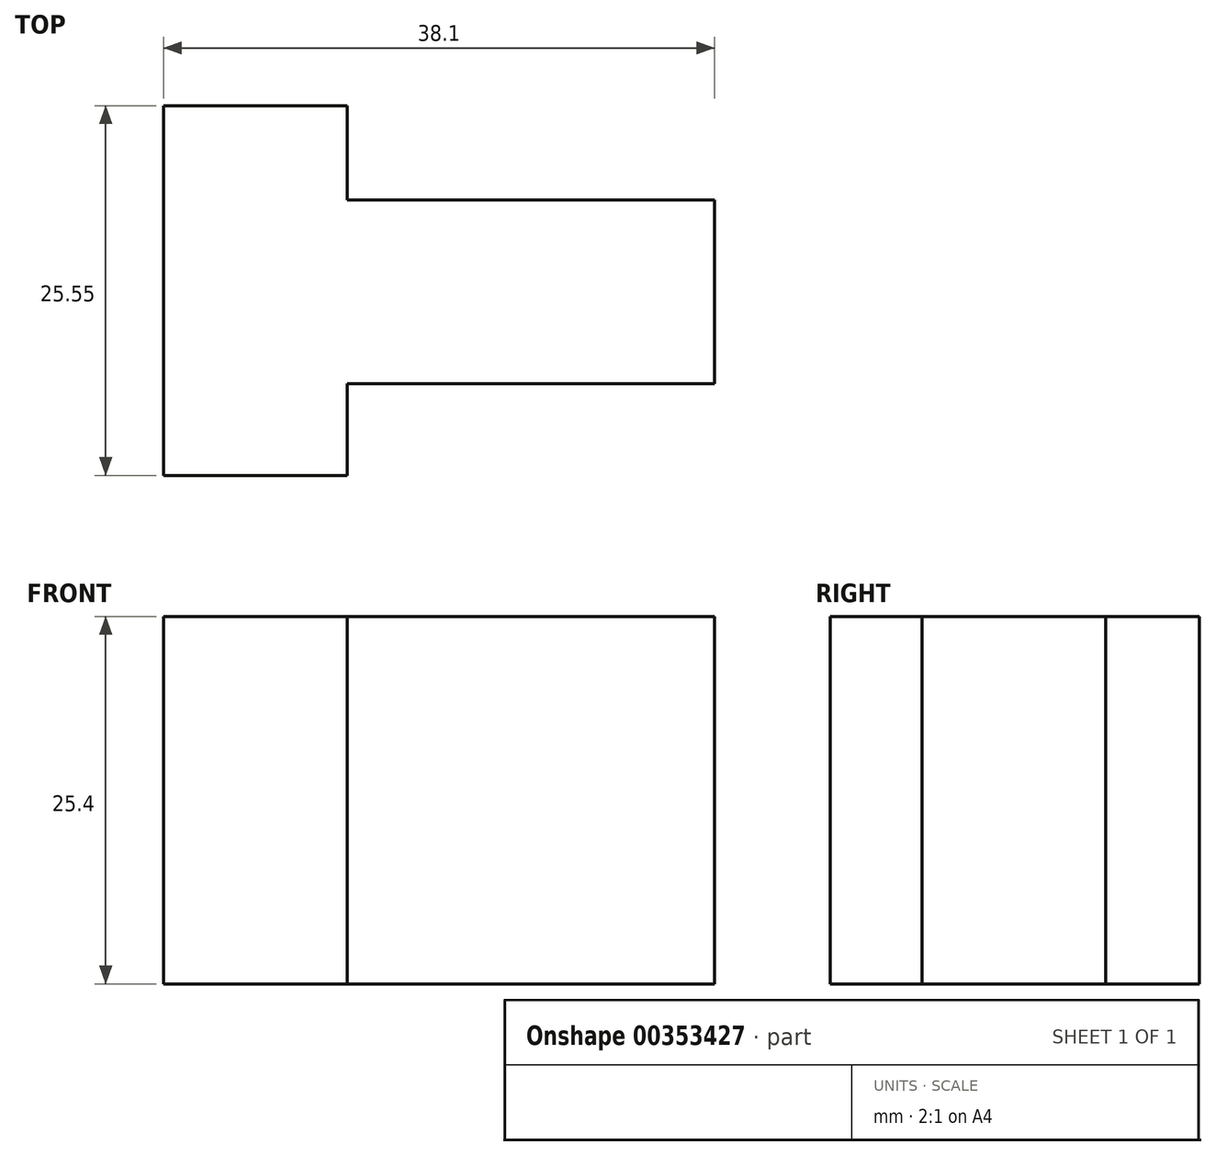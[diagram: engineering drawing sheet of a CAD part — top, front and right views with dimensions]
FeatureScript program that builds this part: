
annotation { "Feature Type Name" : "Feature", "Feature Type Description" : "" }
export const myFeature = defineFeature(function(context is Context, id is Id, definition is map)
    precondition{}
    {
        {
            var Q0;
            Q0=qCreatedBy(makeId("Top.planeOp"),FACE);
            var sketch = newSketch(context, id + "F0", { "sketchPlane" : qUnion([Q0])});
            skLineSegment(sketch, "E0", {"start": v(0, 0) * mm, "end": v(12.7, 0) * mm});
            skLineSegment(sketch, "E1", {"start": v(12.7, 0) * mm, "end": v(12.7, 6.35) * mm});
            skLineSegment(sketch, "E2", {"start": v(12.7, 6.35) * mm, "end": v(38.1, 6.35) * mm});
            skLineSegment(sketch, "E3", {"start": v(38.1, 6.35) * mm, "end": v(38.1, 19.05) * mm});
            skLineSegment(sketch, "E4", {"start": v(38.1, 19.05) * mm, "end": v(12.7, 19.05) * mm});
            skLineSegment(sketch, "E5", {"start": v(12.7, 19.05) * mm, "end": v(12.7, 25.55) * mm});
            skLineSegment(sketch, "E6", {"start": v(12.7, 25.55) * mm, "end": v(0, 25.55) * mm});
            skLineSegment(sketch, "E7", {"start": v(0, 25.55) * mm, "end": v(0, 0) * mm});
            skSolve(sketch);
        }
        {
            var Q0;
            Q0 = qSketchRegion(id + "F0", true);
            extrude(context, id + "F1", {"entities" : qUnion([Q0]), "depth" : 25.4 * mm});
        }
    });
